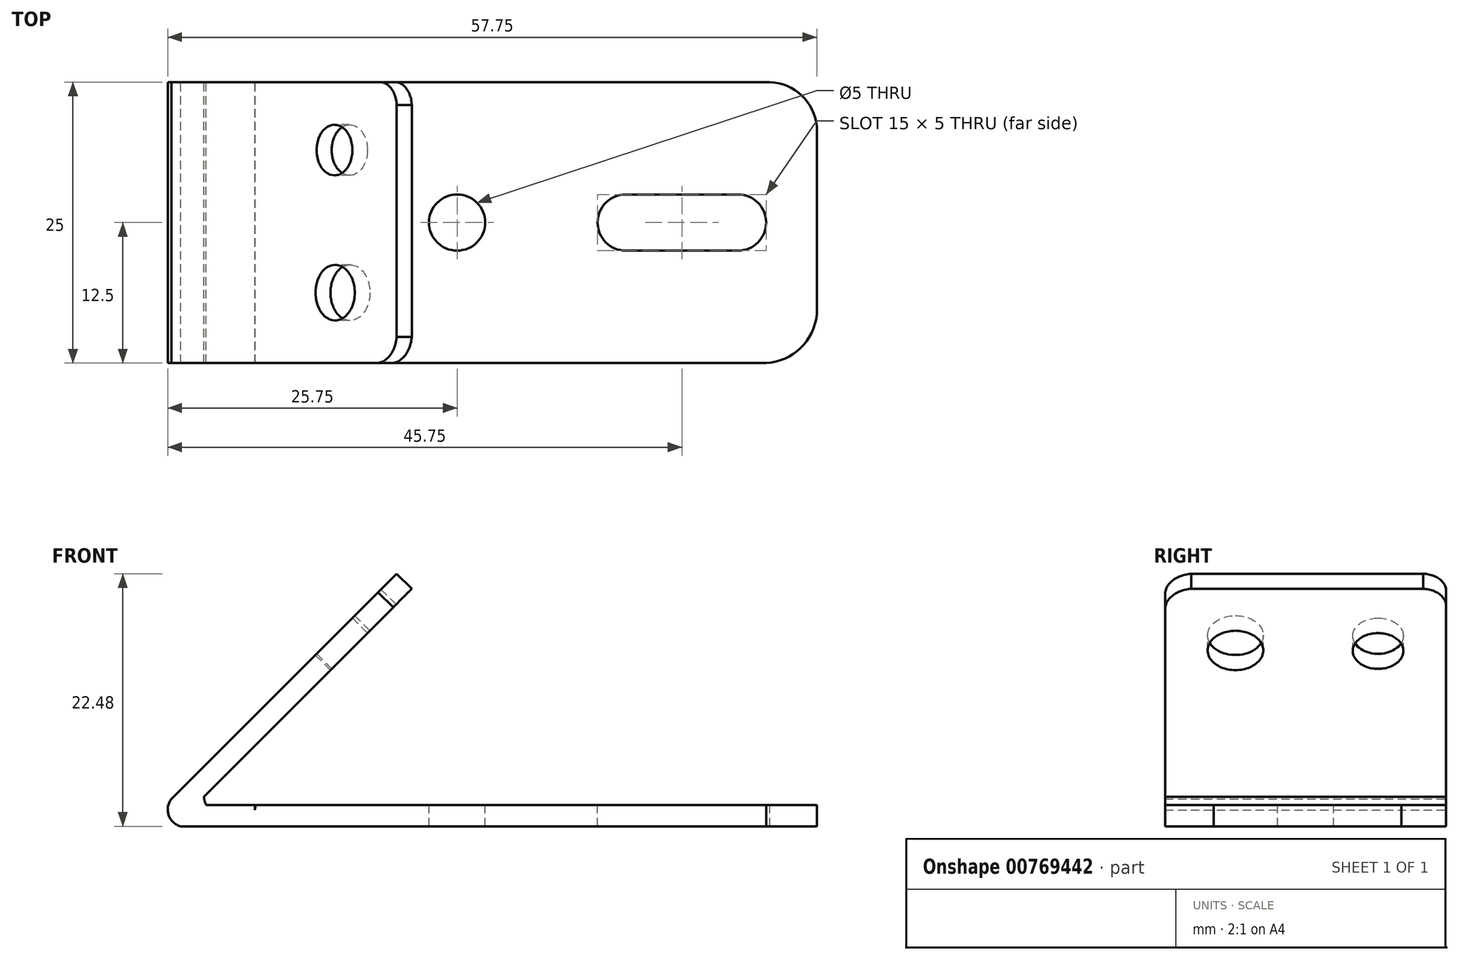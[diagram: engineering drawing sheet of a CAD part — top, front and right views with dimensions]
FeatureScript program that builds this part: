
annotation { "Feature Type Name" : "Feature", "Feature Type Description" : "" }
export const myFeature = defineFeature(function(context is Context, id is Id, definition is map)
    precondition{}
    {
        {
            var Q0;
            Q0=qCreatedBy(makeId("Front.planeOp"),FACE);
            var sketch = newSketch(context, id + "F0", { "sketchPlane" : qUnion([Q0])});
            skLineSegment(sketch, "E0.bottom", {"start": v(0, 0) * mm, "end": v(50, 0) * mm});
            skLineSegment(sketch, "E0.top", {"start": v(0, 1.9) * mm, "end": v(50, 1.9) * mm});
            skLineSegment(sketch, "E0.left", {"start": v(0, 0) * mm, "end": v(0, 1.9) * mm});
            skLineSegment(sketch, "E0.right", {"start": v(50, 0) * mm, "end": v(50, 1.9) * mm});
            skLineSegment(sketch, "E1", {"start": v(0, 1.9) * mm, "end": v(-2.15, 1.9) * mm});
            skArc(sketch, "E2", {"start": v(0, 1.45) * mm, "mid": v(0.03, 1.68) * mm, "end": v(0.05, 1.9) * mm});
            skLineSegment(sketch, "E3", {"start": v(-3.7, 3.46) * mm, "end": v(11.81, 18.98) * mm});
            skLineSegment(sketch, "E4", {"start": v(-3.7, 3.46) * mm, "end": v(13.97, 21.13) * mm});
            skLineSegment(sketch, "E5", {"start": v(13.97, 21.13) * mm, "end": v(12.62, 22.48) * mm});
            skLineSegment(sketch, "E6", {"start": v(12.62, 22.48) * mm, "end": v(-7.4, 2.44) * mm});
            skLineSegment(sketch, "E7", {"start": v(0, 0) * mm, "end": v(-6.6, 0) * mm});
            skLineSegment(sketch, "E8", {"start": v(0.05, 1.9) * mm, "end": v(-4.33, 1.9) * mm});
            skLineSegment(sketch, "E9", {"start": v(-3.7, 3.46) * mm, "end": v(-4.53, 2.64) * mm});
            skArc(sketch, "E10", {"start": v(-4.53, 2.64) * mm, "mid": v(-4.47, 2.26) * mm, "end": v(-4.33, 1.9) * mm});
            skArc(sketch, "E11", {"start": v(-7.18, 2.68) * mm, "mid": v(-7.71, 1.16) * mm, "end": v(-6.6, 0) * mm});
            skSolve(sketch);
        }
        {
            var Q0;
            {var subQ9=sQuery(id+"F0.wireOp",EDGE,"E5");Q0=makeQuery(id+"F0.imprint","IMPRINT",FACE,{"disambiguationData":[TD([[makeQuery(id+"F0.imprint","IMPRINT",EDGE,{"derivedFrom":subQ9}),1.0]])]});}
            var Q1;
            {var subQ1=sQuery(id+"F0.wireOp",EDGE,"E0.bottom");Q1=makeQuery(id+"F0.imprint","IMPRINT",FACE,{"disambiguationData":[TD([[makeQuery(id+"F0.imprint","IMPRINT",EDGE,{"derivedFrom":subQ1}),1.0]])]});}
            extrude(context, id + "F1", {"entities" : qUnion([Q0, Q1]), "depth" : 25 * mm, "offsetDistance" : 25 * mm});
        }
        {
            var Q0;
            Q0=makeQuery(id+"F1.opExtrude","SWEPT_FACE",FACE,{"disambiguationData":[OSD([sQuery(id+"F0.wireOp",EDGE,"E6")])]});
            var sketch = newSketch(context, id + "F2", { "sketchPlane" : qUnion([Q0])});
            skCircle(sketch, "E12", {"center": v(6.05, 17) * mm, "radius": 2.25 * mm});
            skCircle(sketch, "E13", {"center": v(18.74, 17.07) * mm, "radius": 2.48 * mm});
            skSolve(sketch);
        }
        {
            var Q0;
            Q0=makeQuery(id+"F2.imprint","IMPRINT",FACE,{"disambiguationData":[TD([[makeQuery(id+"F2.imprint","IMPRINT",EDGE,{"derivedFrom":sQuery(id+"F2.wireOp",EDGE,"E13")}),1.0]])]});
            var Q1;
            Q1=makeQuery(id+"F2.imprint","IMPRINT",FACE,{"disambiguationData":[TD([[makeQuery(id+"F2.imprint","IMPRINT",EDGE,{"derivedFrom":sQuery(id+"F2.wireOp",EDGE,"E12")}),1.0]])]});
            extrude(context, id + "F3", {"entities" : qUnion([Q0, Q1]), "operationType" : NewBodyOperationType.REMOVE, "oppositeDirection" : true, "depth" : 5 * mm, "offsetDistance" : 25 * mm});
        }
        {
            var Q0;
            Q0=makeQuery(id+"F1.opExtrude","SWEPT_FACE",FACE,{"disambiguationData":[OSD([sQuery(id+"F0.wireOp",EDGE,"E6")])]});
            var sketch = newSketch(context, id + "F4", { "sketchPlane" : qUnion([Q0])});
            skArc(sketch, "E14", {"start": v(25, 21.9) * mm, "mid": v(24.44, 23.84) * mm, "end": v(22.67, 24.82) * mm});
            skArc(sketch, "E15", {"start": v(2.23, 24.82) * mm, "mid": v(0.72, 24.29) * mm, "end": v(0, 22.85) * mm});
            skSolve(sketch);
        }
        {
            var Q0;
            {var subQ0=sQuery(id+"F4.wireOp",EDGE,"E15");var subQ1=sQuery(id+"F0.wireOp",EDGE,"E6");var subQ2=makeQuery(id+"F1.opExtrude","CAP_EDGE",EDGE,{"disambiguationData":[OSD([subQ1])],"isStart":true});var subQ3=makeQuery(id+"F4.imprint","INTERSECT",VERTEX,{"derivedFrom":[subQ2,subQ0]});Q0=makeQuery(id+"F4.imprint","IMPRINT",FACE,{"disambiguationData":[TD([[makeQuery(id+"F4.imprint","IMPRINT",EDGE,{"disambiguationData":[TD([[subQ3,1.0]])],"derivedFrom":subQ0}),-1.0]])]});}
            var Q1;
            {var subQ0=sQuery(id+"F4.wireOp",EDGE,"E14");var subQ1=sQuery(id+"F0.wireOp",EDGE,"E6");var subQ4=makeQuery(id+"F1.opExtrude","CAP_EDGE",EDGE,{"disambiguationData":[OSD([subQ1])],"isStart":false});var subQ5=makeQuery(id+"F4.imprint","INTERSECT",VERTEX,{"disambiguationData":[OD(1.0)],"derivedFrom":[subQ4,subQ0]});Q1=makeQuery(id+"F4.imprint","IMPRINT",FACE,{"disambiguationData":[TD([[makeQuery(id+"F4.imprint","IMPRINT",EDGE,{"disambiguationData":[TD([[subQ5,-1.0]])],"derivedFrom":subQ0}),-1.0]])]});}
            extrude(context, id + "F5", {"entities" : qUnion([Q0, Q1]), "operationType" : NewBodyOperationType.REMOVE, "oppositeDirection" : true, "depth" : 6 * mm, "offsetDistance" : 25 * mm});
        }
        {
            var Q0;
            Q0=makeQuery(id+"F1.opExtrude","SWEPT_FACE",FACE,{"disambiguationData":[OSD([sQuery(id+"F0.wireOp",EDGE,"E0.top")])]});
            var sketch = newSketch(context, id + "F6", { "sketchPlane" : qUnion([Q0])});
            skArc(sketch, "E16", {"start": v(43, -15) * mm, "mid": v(45.5, -12.5) * mm, "end": v(43, -10) * mm});
            skArc(sketch, "E17", {"start": v(33, -10) * mm, "mid": v(30.5, -12.5) * mm, "end": v(33, -15) * mm});
            skLineSegment(sketch, "E18", {"start": v(33, -10) * mm, "end": v(43, -10) * mm});
            skLineSegment(sketch, "E19", {"start": v(33, -15) * mm, "end": v(43, -15) * mm});
            skPoint(sketch, "E20.orphan", {"position": v(50, -12.5) * mm});
            skCircle(sketch, "E21", {"center": v(18, -12.5) * mm, "radius": 2.5 * mm});
            skArc(sketch, "E22", {"start": v(45.5, -25) * mm, "mid": v(48.55, -23.68) * mm, "end": v(50, -20.68) * mm});
            skArc(sketch, "E23", {"start": v(50, -4.75) * mm, "mid": v(48.82, -1.36) * mm, "end": v(45.5, 0) * mm});
            skPoint(sketch, "E24.end.orphan", {"position": v(45.5, -12.5) * mm});
            skPoint(sketch, "E25.trimOffspring.end.orphan", {"position": v(0, -12.5) * mm});
            skSolve(sketch);
        }
        {
            var Q0;
            {var subQ0=sQuery(id+"F6.wireOp",EDGE,"E23");var subQ1=sQuery(id+"F0.wireOp",EDGE,"E0.top");var subQ4=makeQuery(id+"F1.opExtrude","CAP_EDGE",EDGE,{"disambiguationData":[OSD([subQ1])],"isStart":true});var subQ5=makeQuery(id+"F6.imprint","INTERSECT",VERTEX,{"disambiguationData":[OD(1.0)],"derivedFrom":[subQ4,subQ0]});Q0=makeQuery(id+"F6.imprint","IMPRINT",FACE,{"disambiguationData":[TD([[makeQuery(id+"F6.imprint","IMPRINT",EDGE,{"disambiguationData":[TD([[subQ5,1.0]])],"derivedFrom":subQ0}),-1.0]])]});}
            var Q1;
            {var subQ0=sQuery(id+"F6.wireOp",EDGE,"E22");Q1=makeQuery(id+"F6.imprint","IMPRINT",FACE,{"disambiguationData":[TD([[makeQuery(id+"F6.imprint","IMPRINT",EDGE,{"derivedFrom":subQ0}),-1.0]])]});}
            var Q2;
            Q2=makeQuery(id+"F6.imprint","IMPRINT",FACE,{"disambiguationData":[TD([[makeQuery(id+"F6.imprint","IMPRINT",EDGE,{"derivedFrom":sQuery(id+"F6.wireOp",EDGE,"E16")}),1.0]])]});
            var Q3;
            Q3=makeQuery(id+"F6.imprint","IMPRINT",FACE,{"disambiguationData":[TD([[makeQuery(id+"F6.imprint","IMPRINT",EDGE,{"derivedFrom":sQuery(id+"F6.wireOp",EDGE,"E21")}),1.0]])]});
            extrude(context, id + "F7", {"entities" : qUnion([Q0, Q1, Q2, Q3]), "operationType" : NewBodyOperationType.REMOVE, "oppositeDirection" : true, "depth" : 25 * mm, "offsetDistance" : 25 * mm});
        }
    });
